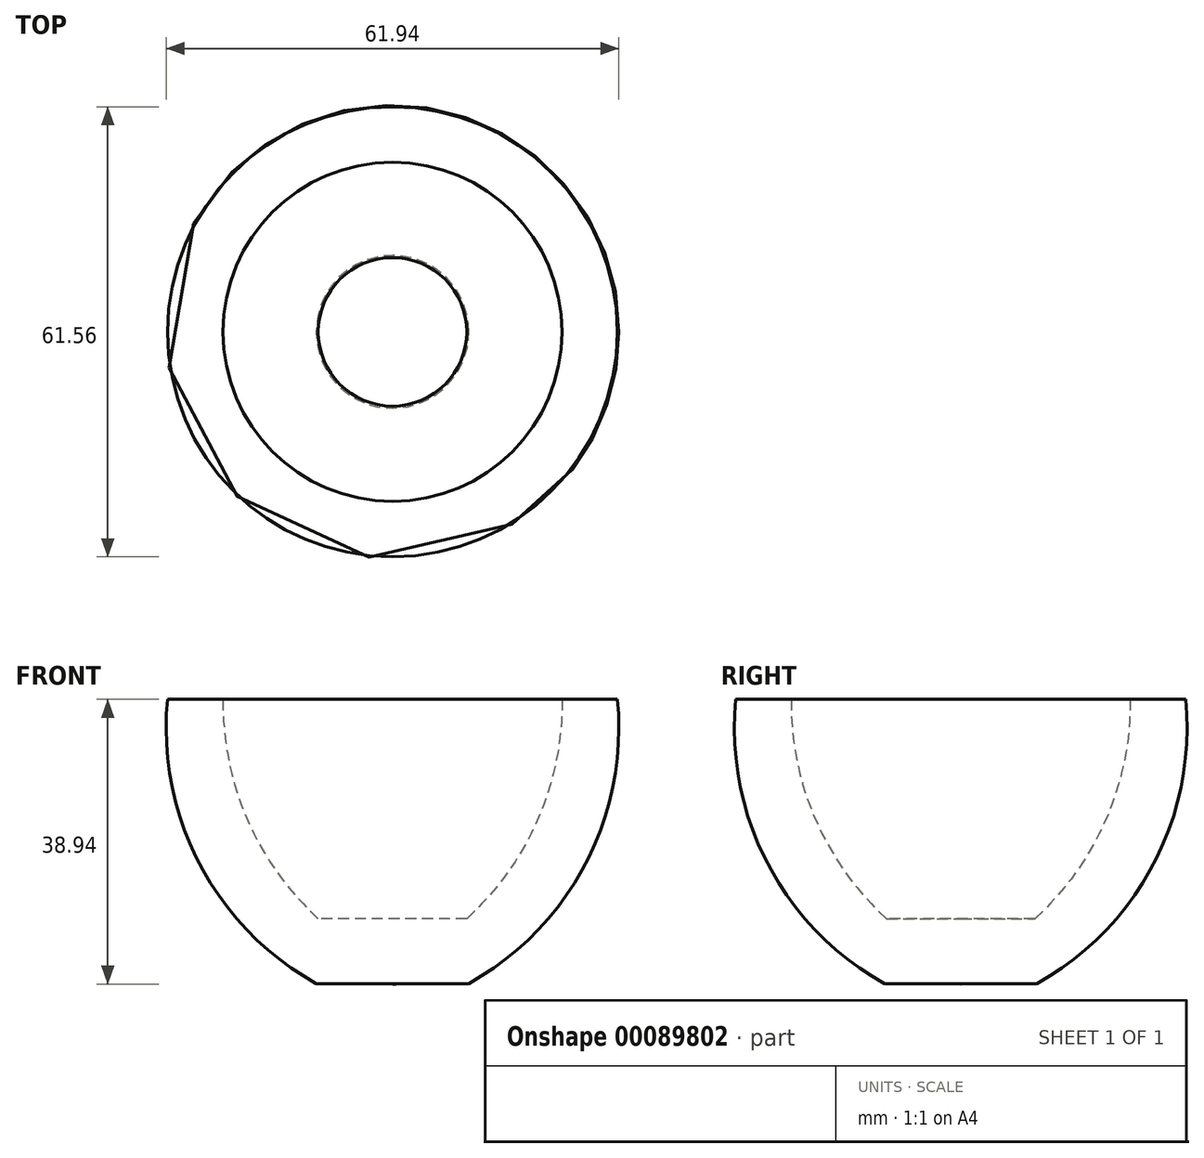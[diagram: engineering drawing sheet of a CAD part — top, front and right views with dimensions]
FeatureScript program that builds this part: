
annotation { "Feature Type Name" : "Feature", "Feature Type Description" : "" }
export const myFeature = defineFeature(function(context is Context, id is Id, definition is map)
    precondition{}
    {
        {
            var Q0;
            Q0=qCreatedBy(makeId("Front.planeOp"),FACE);
            var sketch = newSketch(context, id + "F0", { "sketchPlane" : qUnion([Q0])});
            skPoint(sketch, "E0.oppositeSnap0", {"position": v(7.13, -28.44) * mm});
            skArc(sketch, "E1", {"start": v(10.16, -30) * mm, "mid": v(19.88, -16.4) * mm, "end": v(23.2, 0) * mm});
            skLineSegment(sketch, "E2", {"start": v(10.16, -30) * mm, "end": v(0, -30) * mm});
            skArc(sketch, "E3", {"start": v(10.44, -38.88) * mm, "mid": v(26.41, -22.48) * mm, "end": v(30.78, 0) * mm});
            skLineSegment(sketch, "E4", {"start": v(30.78, 0) * mm, "end": v(23.2, 0) * mm});
            skLineSegment(sketch, "E5", {"start": v(0, -30) * mm, "end": v(0, -38.94) * mm});
            skLineSegment(sketch, "E6", {"start": v(10.44, -38.88) * mm, "end": v(0, -38.94) * mm});
            skLineSegment(sketch, "E7", {"start": v(0, 0) * mm, "end": v(0, -38.94) * mm, "construction": true});
            skSolve(sketch);
        }
        {
            var Q0;
            Q0=makeQuery(id+"F0.imprint","IMPRINT",FACE,{"disambiguationData":[TD([[makeQuery(id+"F0.imprint","IMPRINT",EDGE,{"derivedFrom":sQuery(id+"F0.wireOp",EDGE,"E1")}),-1.0]])]});
            var Q1;
            Q1=sQuery(id+"F0.wireOp",EDGE,"E7");
            revolve(context, id + "F1", {"entities" : qUnion([Q0]), "axis" : qUnion([Q1]), "revolveType" : RevolveType.FULL});
        }
    });
